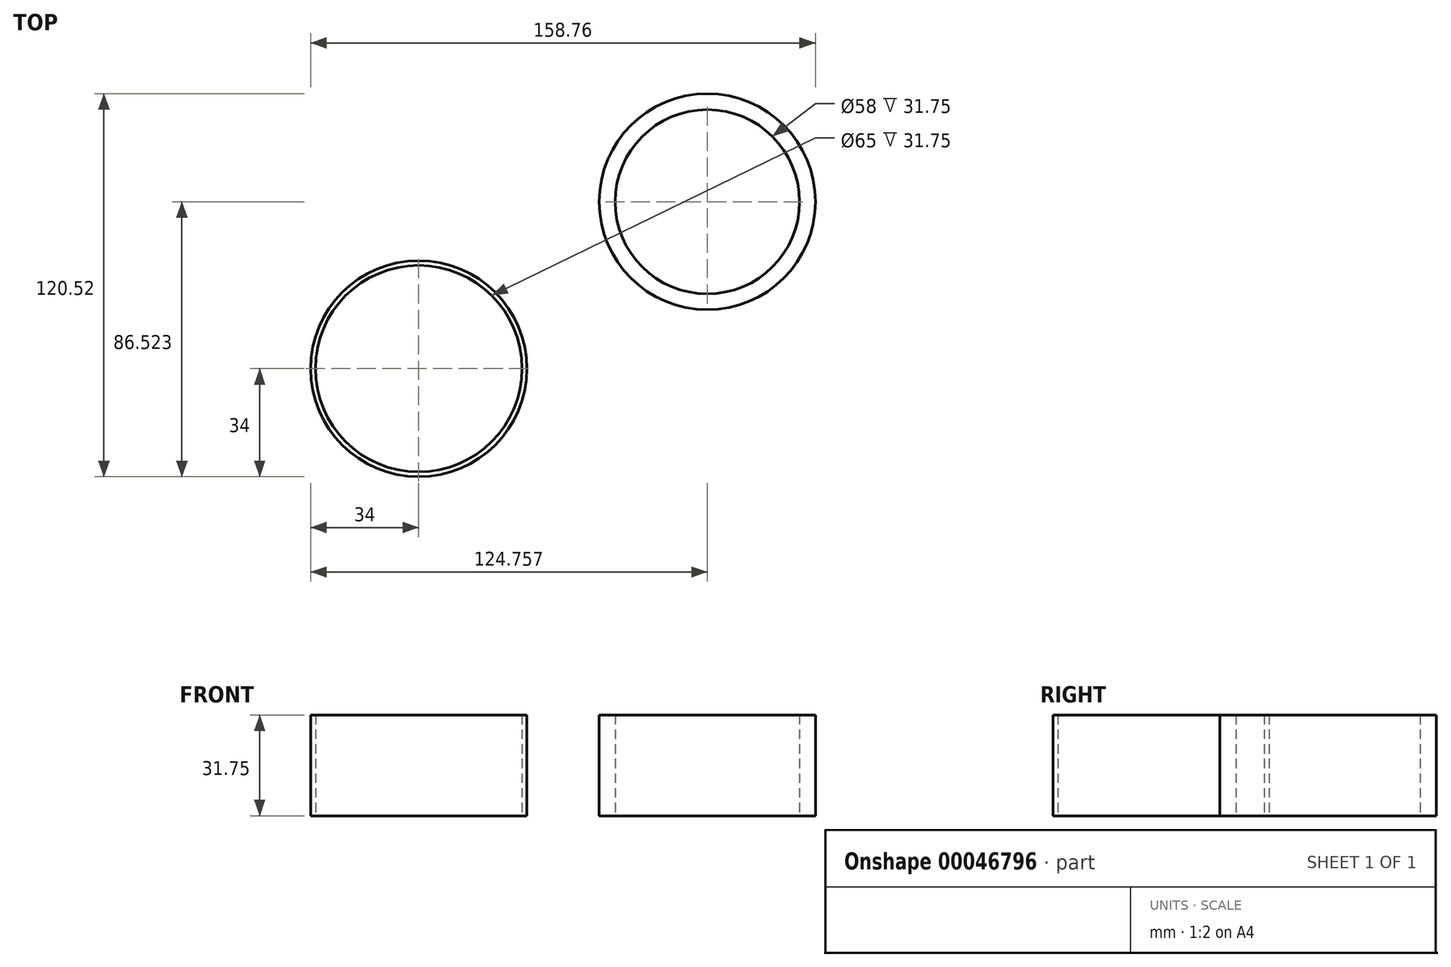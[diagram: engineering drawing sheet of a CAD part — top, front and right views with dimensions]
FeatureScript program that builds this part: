
annotation { "Feature Type Name" : "Feature", "Feature Type Description" : "" }
export const myFeature = defineFeature(function(context is Context, id is Id, definition is map)
    precondition{}
    {
        {
            var Q0;
            Q0=qCreatedBy(makeId("Top.planeOp"),FACE);
            var sketch = newSketch(context, id + "F0", { "sketchPlane" : qUnion([Q0])});
            skCircle(sketch, "E0", {"center": v(0, 0) * mm, "radius": 32.5 * mm});
            skCircle(sketch, "E1", {"center": v(0, 0) * mm, "radius": 34 * mm});
            skSolve(sketch);
        }
        {
            var Q0;
            Q0 = qSketchRegion(id + "F0", true);
            extrude(context, id + "F1", {"entities" : qUnion([Q0]), "depth" : 31.75 * mm, "offsetDistance" : 25.4 * mm});
        }
        {
            var Q0;
            Q0=qCreatedBy(makeId("Top.planeOp"),FACE);
            var sketch = newSketch(context, id + "F2", { "sketchPlane" : qUnion([Q0])});
            skCircle(sketch, "E2", {"center": v(90.76, 52.52) * mm, "radius": 34 * mm});
            skCircle(sketch, "E3", {"center": v(90.76, 52.52) * mm, "radius": 29 * mm});
            skSolve(sketch);
        }
        {
            var Q0;
            Q0 = qSketchRegion(id + "F2", true);
            extrude(context, id + "F3", {"entities" : qUnion([Q0]), "depth" : 31.75 * mm, "offsetDistance" : 25.4 * mm});
        }
    });
